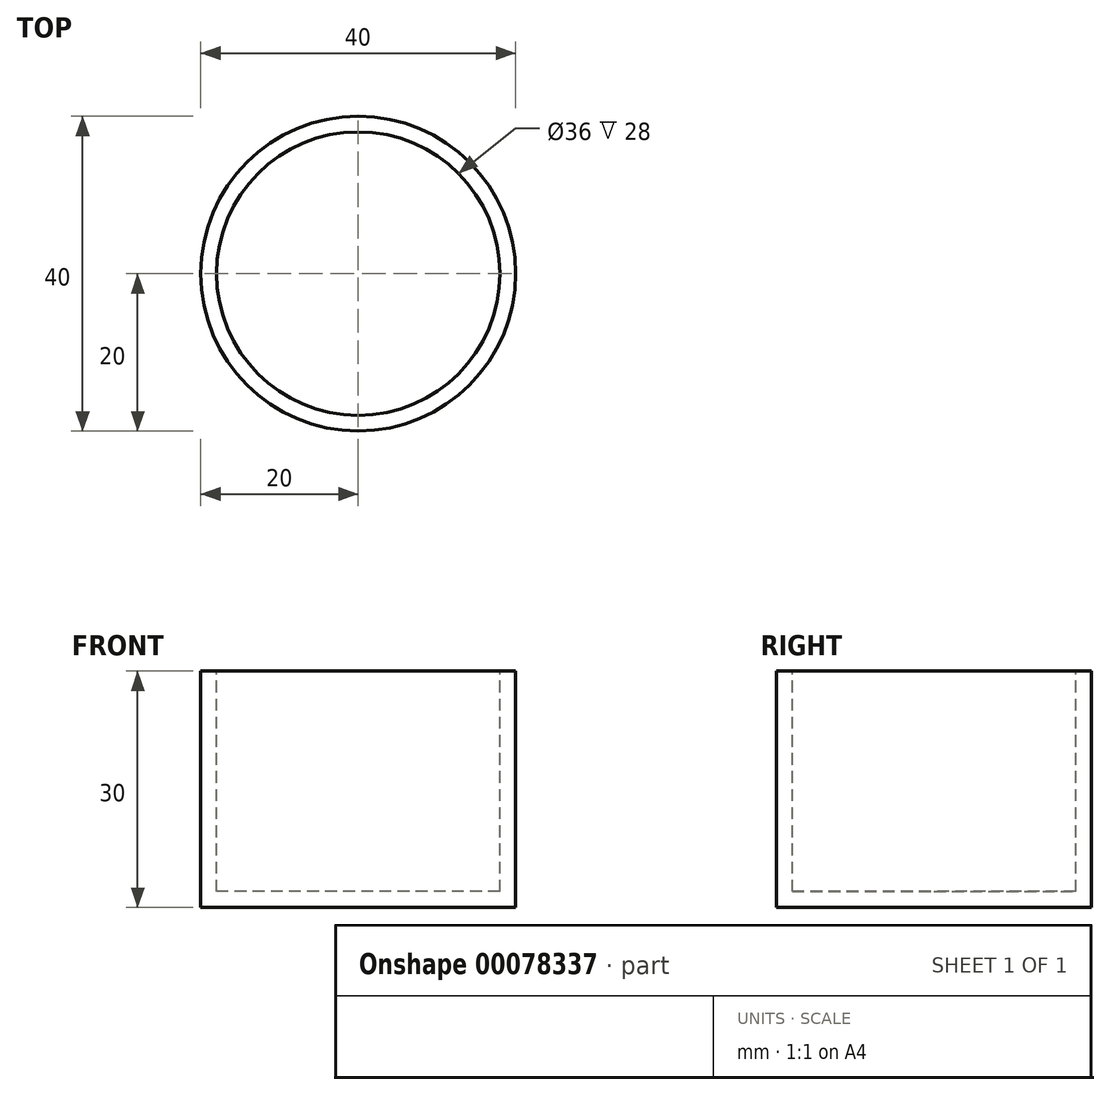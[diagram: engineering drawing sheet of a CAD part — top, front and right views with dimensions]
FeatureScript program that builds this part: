
annotation { "Feature Type Name" : "Feature", "Feature Type Description" : "" }
export const myFeature = defineFeature(function(context is Context, id is Id, definition is map)
    precondition{}
    {
        {
            var Q0;
            Q0=qCreatedBy(makeId("Right.planeOp"),FACE);
            var sketch = newSketch(context, id + "F0", { "sketchPlane" : qUnion([Q0])});
            skLineSegment(sketch, "E0", {"start": v(0, 0) * mm, "end": v(-20, 0) * mm});
            skLineSegment(sketch, "E1", {"start": v(-20, 0) * mm, "end": v(-20, 30) * mm});
            skLineSegment(sketch, "E2", {"start": v(-20, 30) * mm, "end": v(0, 30) * mm});
            skLineSegment(sketch, "E3", {"start": v(0, 30) * mm, "end": v(0, 0) * mm});
            skSolve(sketch);
        }
        {
            var Q0;
            Q0 = qSketchRegion(id + "F0", true);
            var Q1;
            Q1=sQuery(id+"F0.wireOp",EDGE,"E3");
            revolve(context, id + "F1", {"entities" : qUnion([Q0]), "axis" : qUnion([Q1]), "revolveType" : RevolveType.FULL});
        }
        {
            var Q0;
            Q0=makeQuery(id+"F1.opRevolve","SWEPT_FACE",FACE,{"disambiguationData":[OSD([sQuery(id+"F0.wireOp",EDGE,"E2")])]});
            shell(context, id + "F2", {"entities" : qUnion([Q0]), "thickness" : 2 * mm});
        }
    });
